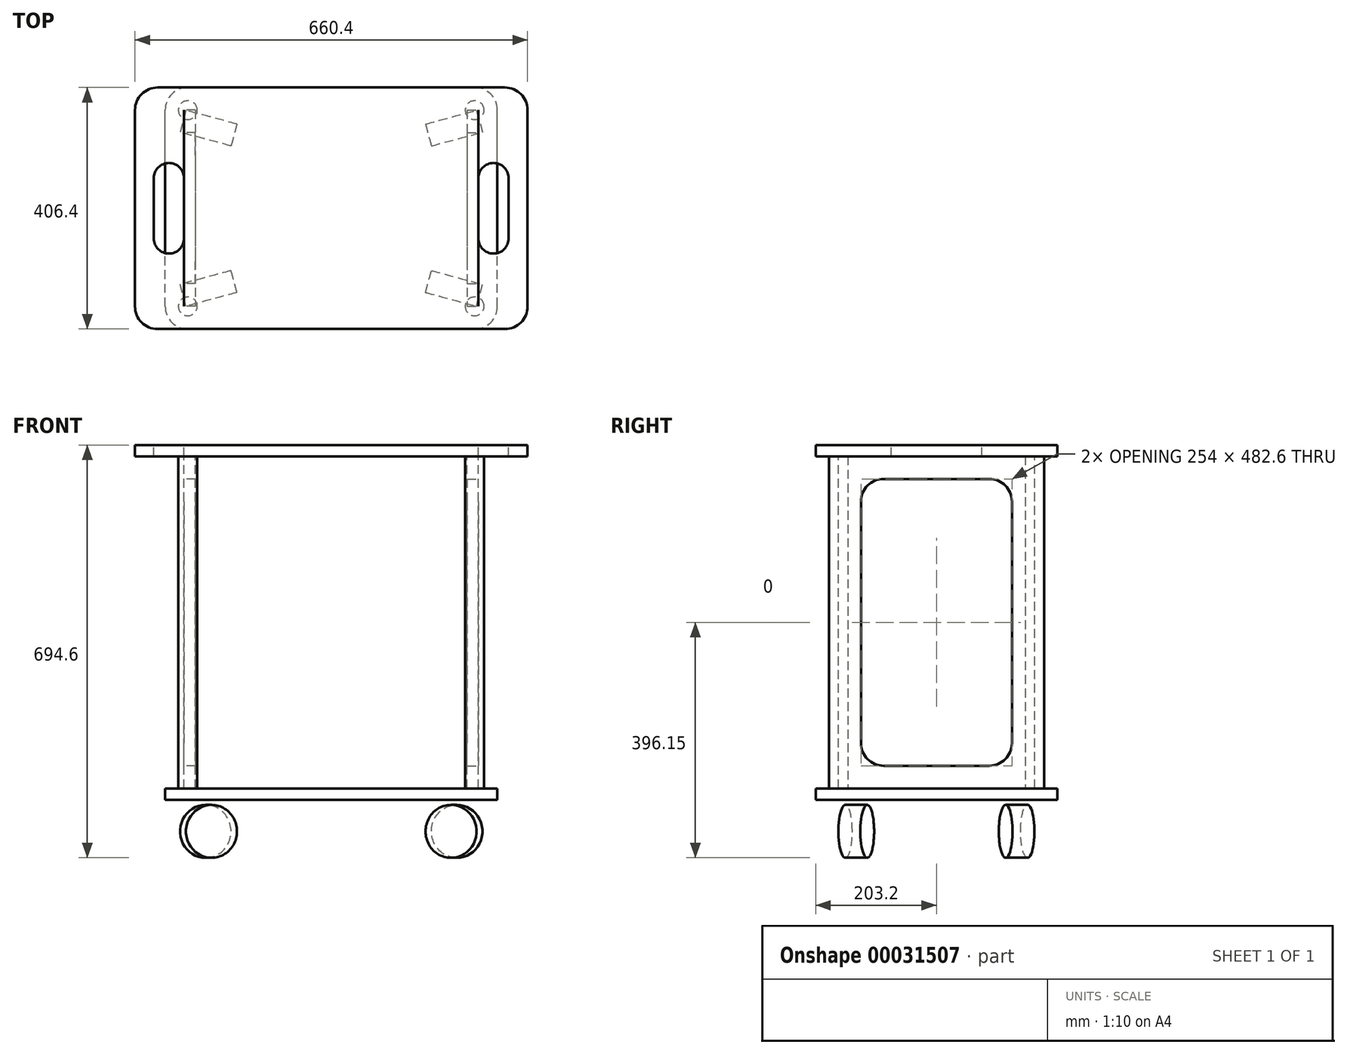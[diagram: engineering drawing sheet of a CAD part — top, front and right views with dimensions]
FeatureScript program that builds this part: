
annotation { "Feature Type Name" : "Feature", "Feature Type Description" : "" }
export const myFeature = defineFeature(function(context is Context, id is Id, definition is map)
    precondition{}
    {
        {
            var Q0;
            Q0=qCreatedBy(makeId("Top.planeOp"),FACE);
            var sketch = newSketch(context, id + "F0", { "sketchPlane" : qUnion([Q0])});
            skLineSegment(sketch, "E0.rect.bottom", {"start": v(241.3, -203.2) * mm, "end": v(-241.3, -203.2) * mm});
            skLineSegment(sketch, "E0.rect.top", {"start": v(241.3, 203.2) * mm, "end": v(-241.3, 203.2) * mm});
            skLineSegment(sketch, "E0.rect.left", {"start": v(279.4, -165.1) * mm, "end": v(279.4, 165.1) * mm});
            skLineSegment(sketch, "E0.rect.right", {"start": v(-279.4, -165.1) * mm, "end": v(-279.4, 165.1) * mm});
            skPoint(sketch, "E0.rect.middle", {"position": v(0, 0) * mm});
            skPoint(sketch, "E1.visualSharp", {"position": v(-279.4, 203.2) * mm});
            skArc(sketch, "E1.filletArc", {"start": v(-241.3, 203.2) * mm, "mid": v(-268.24, 192.04) * mm, "end": v(-279.4, 165.1) * mm});
            skPoint(sketch, "E2.visualSharp", {"position": v(-279.4, -203.2) * mm});
            skArc(sketch, "E2.filletArc", {"start": v(-279.4, -165.1) * mm, "mid": v(-268.24, -192.04) * mm, "end": v(-241.3, -203.2) * mm});
            skPoint(sketch, "E3.visualSharp", {"position": v(279.4, -203.2) * mm});
            skArc(sketch, "E3.filletArc", {"start": v(241.3, -203.2) * mm, "mid": v(268.24, -192.04) * mm, "end": v(279.4, -165.1) * mm});
            skPoint(sketch, "E4.visualSharp", {"position": v(279.4, 203.2) * mm});
            skArc(sketch, "E4.filletArc", {"start": v(279.4, 165.1) * mm, "mid": v(268.24, 192.04) * mm, "end": v(241.3, 203.2) * mm});
            skSolve(sketch);
        }
        {
            var Q0;
            Q0=makeQuery(id+"F0.imprint","IMPRINT",FACE,{"disambiguationData":[TD([[makeQuery(id+"F0.imprint","IMPRINT",EDGE,{"derivedFrom":sQuery(id+"F0.wireOp",EDGE,"E0.rect.bottom")}),-1.0]])]});
            extrude(context, id + "F1", {"entities" : qUnion([Q0]), "depth" : 19.05 * mm});
        }
        {
            var Q0;
            Q0=makeQuery(id+"F1.opExtrude","CAP_FACE",FACE,{"disambiguationData":[OSD([sQuery(id+"F0.wireOp",EDGE,"E0.rect.bottom"),sQuery(id+"F0.wireOp",EDGE,"E0.rect.top"),sQuery(id+"F0.wireOp",EDGE,"E0.rect.left"),sQuery(id+"F0.wireOp",EDGE,"E0.rect.right"),sQuery(id+"F0.wireOp",EDGE,"E1.filletArc"),sQuery(id+"F0.wireOp",EDGE,"E2.filletArc"),sQuery(id+"F0.wireOp",EDGE,"E3.filletArc"),sQuery(id+"F0.wireOp",EDGE,"E4.filletArc")])],"isStart":false});
            var sketch = newSketch(context, id + "F2", { "sketchPlane" : qUnion([Q0])});
            skSolve(sketch);
        }
        {
            var Q0;
            Q0=makeQuery(id+"F2.imprint","IMPRINT",FACE,{"disambiguationData":[TD([[makeQuery(id+"F2.imprint","IMPRINT",EDGE,{"derivedFrom":makeQuery(id+"F1.opExtrude","CAP_EDGE",EDGE,{"disambiguationData":[OSD([sQuery(id+"F0.wireOp",EDGE,"E0.rect.bottom")])],"isStart":false})}),-1.0]])]});
            var sketch = newSketch(context, id + "F3", { "sketchPlane" : qUnion([Q0])});
            skLineSegment(sketch, "E5", {"start": v(0, 0) * mm, "end": v(-247.65, 0) * mm});
            skSolve(sketch);
        }
        {
            var Q0;
            Q0=sQuery(id+"F3.wireOp",EDGE,"E5");
            var Q1;
            Q1=sQuery(id+"F3.wireOp",VERTEX,"E5.end");
            cPlane(context, id + "F4", {"entities" : qUnion([Q0, Q1]), "cplaneType" : CPlaneType.CURVE_POINT, "offset" : 152.4 * mm, "width" : 152.4 * mm, "height" : 152.4 * mm});
        }
        {
            var Q0;
            Q0=qCreatedBy(id+"F4.planeOp",FACE);
            var sketch = newSketch(context, id + "F5", { "sketchPlane" : qUnion([Q0])});
            skLineSegment(sketch, "E6.bottom", {"start": v(-165.1, 19.05) * mm, "end": v(165.1, 19.05) * mm});
            skLineSegment(sketch, "E6.top", {"start": v(-165.1, 577.85) * mm, "end": v(165.1, 577.85) * mm});
            skLineSegment(sketch, "E6.left", {"start": v(-165.1, 19.05) * mm, "end": v(-165.1, 577.85) * mm});
            skLineSegment(sketch, "E6.right", {"start": v(165.1, 19.05) * mm, "end": v(165.1, 577.85) * mm});
            skSolve(sketch);
        }
        {
            var Q0;
            Q0 = qSketchRegion(id + "F5", true);
            extrude(context, id + "F6", {"entities" : qUnion([Q0]), "oppositeDirection" : true, "depth" : 19.05 * mm});
        }
        {
            var Q0;
            Q0=makeQuery(id+"F6.opExtrude","CAP_FACE",FACE,{"disambiguationData":[OSD([sQuery(id+"F5.wireOp",EDGE,"E6.bottom"),sQuery(id+"F5.wireOp",EDGE,"E6.top"),sQuery(id+"F5.wireOp",EDGE,"E6.left"),sQuery(id+"F5.wireOp",EDGE,"E6.right")])],"isStart":true});
            var sketch = newSketch(context, id + "F7", { "sketchPlane" : qUnion([Q0])});
            skLineSegment(sketch, "E7.bottom", {"start": v(-88.9, 539.75) * mm, "end": v(88.9, 539.75) * mm});
            skLineSegment(sketch, "E7.top", {"start": v(-88.9, 57.15) * mm, "end": v(88.9, 57.15) * mm});
            skLineSegment(sketch, "E7.left", {"start": v(-127, 501.65) * mm, "end": v(-127, 95.25) * mm});
            skLineSegment(sketch, "E7.right", {"start": v(127, 501.65) * mm, "end": v(127, 95.25) * mm});
            skPoint(sketch, "E8.visualSharp", {"position": v(-127, 539.75) * mm});
            skArc(sketch, "E8.filletArc", {"start": v(-88.9, 539.75) * mm, "mid": v(-115.84, 528.6) * mm, "end": v(-127, 501.65) * mm});
            skPoint(sketch, "E9.visualSharp", {"position": v(127, 539.75) * mm});
            skArc(sketch, "E9.filletArc", {"start": v(127, 501.65) * mm, "mid": v(115.84, 528.6) * mm, "end": v(88.9, 539.75) * mm});
            skPoint(sketch, "E10.visualSharp", {"position": v(127, 57.15) * mm});
            skArc(sketch, "E10.filletArc", {"start": v(88.9, 57.15) * mm, "mid": v(115.84, 68.3) * mm, "end": v(127, 95.25) * mm});
            skPoint(sketch, "E11.visualSharp", {"position": v(-127, 57.15) * mm});
            skArc(sketch, "E11.filletArc", {"start": v(-127, 95.25) * mm, "mid": v(-115.84, 68.3) * mm, "end": v(-88.9, 57.15) * mm});
            skSolve(sketch);
        }
        {
            var Q0;
            Q0=makeQuery(id+"F7.imprint","IMPRINT",FACE,{"disambiguationData":[TD([[makeQuery(id+"F7.imprint","IMPRINT",EDGE,{"derivedFrom":sQuery(id+"F7.wireOp",EDGE,"E7.bottom")}),-1.0]])]});
            extrude(context, id + "F8", {"entities" : qUnion([Q0]), "operationType" : NewBodyOperationType.REMOVE, "endBound" : BoundingType.THROUGH_ALL, "oppositeDirection" : true, "depth" : 25.4 * mm});
        }
        {
            var Q0;
            Q0=makeQuery(id+"F1.opExtrude","SWEPT_BODY",BODY,{"disambiguationData":[OSD([sQuery(id+"F0.wireOp",EDGE,"E0.rect.bottom"),sQuery(id+"F0.wireOp",EDGE,"E0.rect.top"),sQuery(id+"F0.wireOp",EDGE,"E0.rect.left"),sQuery(id+"F0.wireOp",EDGE,"E0.rect.right"),sQuery(id+"F0.wireOp",EDGE,"E1.filletArc"),sQuery(id+"F0.wireOp",EDGE,"E2.filletArc"),sQuery(id+"F0.wireOp",EDGE,"E3.filletArc"),sQuery(id+"F0.wireOp",EDGE,"E4.filletArc")])]});
            var Q1;
            Q1=makeQuery(id+"F6.opExtrude","SWEPT_BODY",BODY,{"disambiguationData":[OSD([sQuery(id+"F5.wireOp",EDGE,"E6.bottom"),sQuery(id+"F5.wireOp",EDGE,"E6.top"),sQuery(id+"F5.wireOp",EDGE,"E6.left"),sQuery(id+"F5.wireOp",EDGE,"E6.right")])]});
            var Q2;
            Q2=qCreatedBy(makeId("Right.planeOp"),FACE);
            mirror(context, id + "F9", {"entities" : qUnion([Q0, Q1]), "mirrorPlane" : qUnion([Q2])});
        }
        {
            var Q0;
            Q0=makeQuery(id+"F6.opExtrude","SWEPT_FACE",FACE,{"disambiguationData":[OSD([sQuery(id+"F5.wireOp",EDGE,"E6.top")])]});
            var sketch = newSketch(context, id + "F10", { "sketchPlane" : qUnion([Q0])});
            skLineSegment(sketch, "E12.rect.bottom", {"start": v(-292.1, -203.2) * mm, "end": v(292.1, -203.2) * mm});
            skLineSegment(sketch, "E12.rect.top", {"start": v(-292.1, 203.2) * mm, "end": v(292.1, 203.2) * mm});
            skLineSegment(sketch, "E12.rect.left", {"start": v(-330.2, -165.1) * mm, "end": v(-330.2, 165.1) * mm});
            skLineSegment(sketch, "E12.rect.right", {"start": v(330.2, -165.1) * mm, "end": v(330.2, 165.1) * mm});
            skPoint(sketch, "E12.rect.middle", {"position": v(0, 0) * mm});
            skPoint(sketch, "E13.visualSharp", {"position": v(-330.2, 203.2) * mm});
            skArc(sketch, "E13.filletArc", {"start": v(-292.1, 203.2) * mm, "mid": v(-319.04, 192.04) * mm, "end": v(-330.2, 165.1) * mm});
            skPoint(sketch, "E14.visualSharp", {"position": v(-330.2, -203.2) * mm});
            skArc(sketch, "E14.filletArc", {"start": v(-330.2, -165.1) * mm, "mid": v(-319.04, -192.04) * mm, "end": v(-292.1, -203.2) * mm});
            skPoint(sketch, "E15.visualSharp", {"position": v(330.2, -203.2) * mm});
            skArc(sketch, "E15.filletArc", {"start": v(292.1, -203.2) * mm, "mid": v(319.04, -192.04) * mm, "end": v(330.2, -165.1) * mm});
            skPoint(sketch, "E16.visualSharp", {"position": v(330.2, 203.2) * mm});
            skArc(sketch, "E16.filletArc", {"start": v(330.2, 165.1) * mm, "mid": v(319.04, 192.04) * mm, "end": v(292.1, 203.2) * mm});
            skSolve(sketch);
        }
        {
            var Q0;
            Q0=makeQuery(id+"F10.imprint","IMPRINT",FACE,{"disambiguationData":[TD([[makeQuery(id+"F10.imprint","IMPRINT",EDGE,{"derivedFrom":sQuery(id+"F10.wireOp",EDGE,"E12.rect.bottom")}),1.0]])]});
            var Q1;
            {var subQ0=sQuery(id+"F5.wireOp",EDGE,"E6.top");Q1=makeQuery(id+"F10.imprint","IMPRINT",FACE,{"disambiguationData":[TD([[makeQuery(id+"F10.imprint","IMPRINT",EDGE,{"derivedFrom":makeQuery(id+"F6.opExtrude","CAP_EDGE",EDGE,{"disambiguationData":[OSD([subQ0])],"isStart":true})}),1.0]])]});}
            extrude(context, id + "F11", {"entities" : qUnion([Q0, Q1]), "depth" : 19.05 * mm});
        }
        {
            var Q0;
            Q0=makeQuery(id+"F11.opExtrude","CAP_FACE",FACE,{"disambiguationData":[OSD([sQuery(id+"F10.wireOp",EDGE,"E12.rect.bottom"),sQuery(id+"F10.wireOp",EDGE,"E12.rect.top"),sQuery(id+"F10.wireOp",EDGE,"E12.rect.left"),sQuery(id+"F10.wireOp",EDGE,"E12.rect.right"),sQuery(id+"F10.wireOp",EDGE,"E13.filletArc"),sQuery(id+"F10.wireOp",EDGE,"E14.filletArc"),sQuery(id+"F10.wireOp",EDGE,"E15.filletArc"),sQuery(id+"F10.wireOp",EDGE,"E16.filletArc")])],"isStart":false});
            var sketch = newSketch(context, id + "F12", { "sketchPlane" : qUnion([Q0])});
            skLineSegment(sketch, "E17.rect.bottom", {"start": v(-273.05, -76.2) * mm, "end": v(-273.05, -76.2) * mm});
            skLineSegment(sketch, "E17.rect.top", {"start": v(-273.05, 76.2) * mm, "end": v(-273.05, 76.2) * mm});
            skLineSegment(sketch, "E17.rect.left", {"start": v(-247.65, -50.8) * mm, "end": v(-247.65, 50.8) * mm});
            skLineSegment(sketch, "E17.rect.right", {"start": v(-298.45, -50.8) * mm, "end": v(-298.45, 50.8) * mm});
            skPoint(sketch, "E17.rect.middle", {"position": v(-273.05, 0) * mm});
            skPoint(sketch, "E18.visualSharp", {"position": v(-298.45, 76.2) * mm});
            skArc(sketch, "E18.filletArc", {"start": v(-273.05, 76.2) * mm, "mid": v(-291.01, 68.76) * mm, "end": v(-298.45, 50.8) * mm});
            skPoint(sketch, "E19.visualSharp", {"position": v(-247.65, 76.2) * mm});
            skArc(sketch, "E19.filletArc", {"start": v(-247.65, 50.8) * mm, "mid": v(-255.09, 68.76) * mm, "end": v(-273.05, 76.2) * mm});
            skPoint(sketch, "E20.visualSharp", {"position": v(-247.65, -76.2) * mm});
            skArc(sketch, "E20.filletArc", {"start": v(-273.05, -76.2) * mm, "mid": v(-255.09, -68.76) * mm, "end": v(-247.65, -50.8) * mm});
            skPoint(sketch, "E21.visualSharp", {"position": v(-298.45, -76.2) * mm});
            skArc(sketch, "E21.filletArc", {"start": v(-298.45, -50.8) * mm, "mid": v(-291.01, -68.76) * mm, "end": v(-273.05, -76.2) * mm});
            skLineSegment(sketch, "E22", {"start": v(0, 0) * mm, "end": v(0, 141.85) * mm, "construction": true});
            skLineSegment(sketch, "E23.MirrorCS", {"start": v(273.05, 76.2) * mm, "end": v(273.05, 76.2) * mm});
            skLineSegment(sketch, "E24.MirrorCS", {"start": v(273.05, -76.2) * mm, "end": v(273.05, -76.2) * mm});
            skArc(sketch, "E25.MirrorCS", {"start": v(273.05, -76.2) * mm, "mid": v(255.09, -68.76) * mm, "end": v(247.65, -50.8) * mm});
            skArc(sketch, "E26.MirrorCS", {"start": v(247.65, 50.8) * mm, "mid": v(255.09, 68.76) * mm, "end": v(273.05, 76.2) * mm});
            skArc(sketch, "E27.MirrorCS", {"start": v(273.05, 76.2) * mm, "mid": v(291.01, 68.76) * mm, "end": v(298.45, 50.8) * mm});
            skArc(sketch, "E28.MirrorCS", {"start": v(298.45, -50.8) * mm, "mid": v(291.01, -68.76) * mm, "end": v(273.05, -76.2) * mm});
            skLineSegment(sketch, "E29.MirrorCS", {"start": v(298.45, -50.8) * mm, "end": v(298.45, 50.8) * mm});
            skLineSegment(sketch, "E30.MirrorCS", {"start": v(247.65, -50.8) * mm, "end": v(247.65, 50.8) * mm});
            skPoint(sketch, "E31.MirrorP", {"position": v(273.05, 0) * mm});
            skPoint(sketch, "E32.MirrorP", {"position": v(298.45, 76.2) * mm});
            skPoint(sketch, "E33.MirrorP", {"position": v(247.65, 76.2) * mm});
            skPoint(sketch, "E34.MirrorP", {"position": v(247.65, -76.2) * mm});
            skPoint(sketch, "E35.MirrorP", {"position": v(298.45, -76.2) * mm});
            skSolve(sketch);
        }
        {
            var Q0;
            Q0 = qSketchRegion(id + "F12", true);
            extrude(context, id + "F13", {"entities" : qUnion([Q0]), "operationType" : NewBodyOperationType.REMOVE, "oppositeDirection" : true, "depth" : 25.4 * mm});
        }
        {
            var Q0;
            Q0=makeQuery(id+"F3.imprint","IMPRINT",FACE,{"disambiguationData":[TD([[makeQuery(id+"F3.imprint","IMPRINT",EDGE,{"derivedFrom":makeQuery(id+"F2.imprint","IMPRINT",EDGE,{"derivedFrom":makeQuery(id+"F1.opExtrude","CAP_EDGE",EDGE,{"disambiguationData":[OSD([sQuery(id+"F0.wireOp",EDGE,"E0.rect.bottom")])],"isStart":false})})}),-1.0]])]});
            var sketch = newSketch(context, id + "F14", { "sketchPlane" : qUnion([Q0])});
            skCircle(sketch, "E36", {"center": v(-241.3, -165.1) * mm, "radius": 15.88 * mm});
            skLineSegment(sketch, "E37", {"start": v(-241.3, -165.1) * mm, "end": v(-241.3, -203.2) * mm, "construction": true});
            skLineSegment(sketch, "E38", {"start": v(-241.3, -165.1) * mm, "end": v(-279.4, -165.1) * mm, "construction": true});
            skLineSegment(sketch, "E39", {"start": v(0, 0) * mm, "end": v(0, -163.09) * mm, "construction": true});
            skLineSegment(sketch, "E40", {"start": v(9.16, 0) * mm, "end": v(136.02, 0) * mm, "construction": true});
            skCircle(sketch, "E41.MirrorC", {"center": v(241.3, -165.1) * mm, "radius": 15.88 * mm});
            skCircle(sketch, "E42.MirrorC", {"center": v(-241.3, 165.1) * mm, "radius": 15.88 * mm});
            skCircle(sketch, "E43.MirrorC", {"center": v(241.3, 165.1) * mm, "radius": 15.88 * mm});
            skSolve(sketch);
        }
        {
            var Q0;
            Q0 = qSketchRegion(id + "F14", true);
            extrude(context, id + "F15", {"entities" : qUnion([Q0]), "depth" : 558.8 * mm});
        }
        {
            var Q0;
            Q0=qCreatedBy(makeId("Top.planeOp"),FACE);
            var sketch = newSketch(context, id + "F16", { "sketchPlane" : qUnion([Q0])});
            skLineSegment(sketch, "E44", {"start": v(-255.07, -45.43) * mm, "end": v(-229.23, -141) * mm});
            skSolve(sketch);
        }
        {
            var Q0;
            Q0=sQuery(id+"F16.wireOp",EDGE,"E44");
            var Q1;
            Q1=sQuery(id+"F16.wireOp",VERTEX,"E44.end");
            cPlane(context, id + "F17", {"entities" : qUnion([Q0, Q1]), "cplaneType" : CPlaneType.CURVE_POINT, "offset" : 152.4 * mm, "width" : 152.4 * mm, "height" : 152.4 * mm});
        }
        {
            var Q0;
            Q0=qCreatedBy(id+"F17.planeOp",FACE);
            var sketch = newSketch(context, id + "F18", { "sketchPlane" : qUnion([Q0])});
            skCircle(sketch, "E45", {"center": v(-234.52, -53.25) * mm, "radius": 44.45 * mm});
            skSolve(sketch);
        }
        {
            var Q0;
            Q0 = qSketchRegion(id + "F18", true);
            extrude(context, id + "F19", {"entities" : qUnion([Q0]), "endBound" : BoundingType.SYMMETRIC, "depth" : 38.1 * mm});
        }
        {
            var Q0;
            Q0=makeQuery(id+"F19.opExtrude","SWEPT_BODY",BODY,{"disambiguationData":[OSD([sQuery(id+"F18.wireOp",EDGE,"E45")])]});
            var Q1;
            Q1=qCreatedBy(makeId("Right.planeOp"),FACE);
            mirror(context, id + "F20", {"entities" : qUnion([Q0]), "mirrorPlane" : qUnion([Q1])});
        }
        {
            var Q0;
            Q0=makeQuery(id+"F19.opExtrude","SWEPT_BODY",BODY,{"disambiguationData":[OSD([sQuery(id+"F18.wireOp",EDGE,"E45")])]});
            var Q1;
            Q1=makeQuery(id+"F20.opPattern","COPY",BODY,{"derivedFrom":makeQuery(id+"F19.opExtrude","SWEPT_BODY",BODY,{"disambiguationData":[OSD([sQuery(id+"F18.wireOp",EDGE,"E45")])]}),"instanceName":"1"});
            var Q2;
            Q2=qCreatedBy(makeId("Front.planeOp"),FACE);
            mirror(context, id + "F21", {"entities" : qUnion([Q0, Q1]), "mirrorPlane" : qUnion([Q2])});
        }
    });
